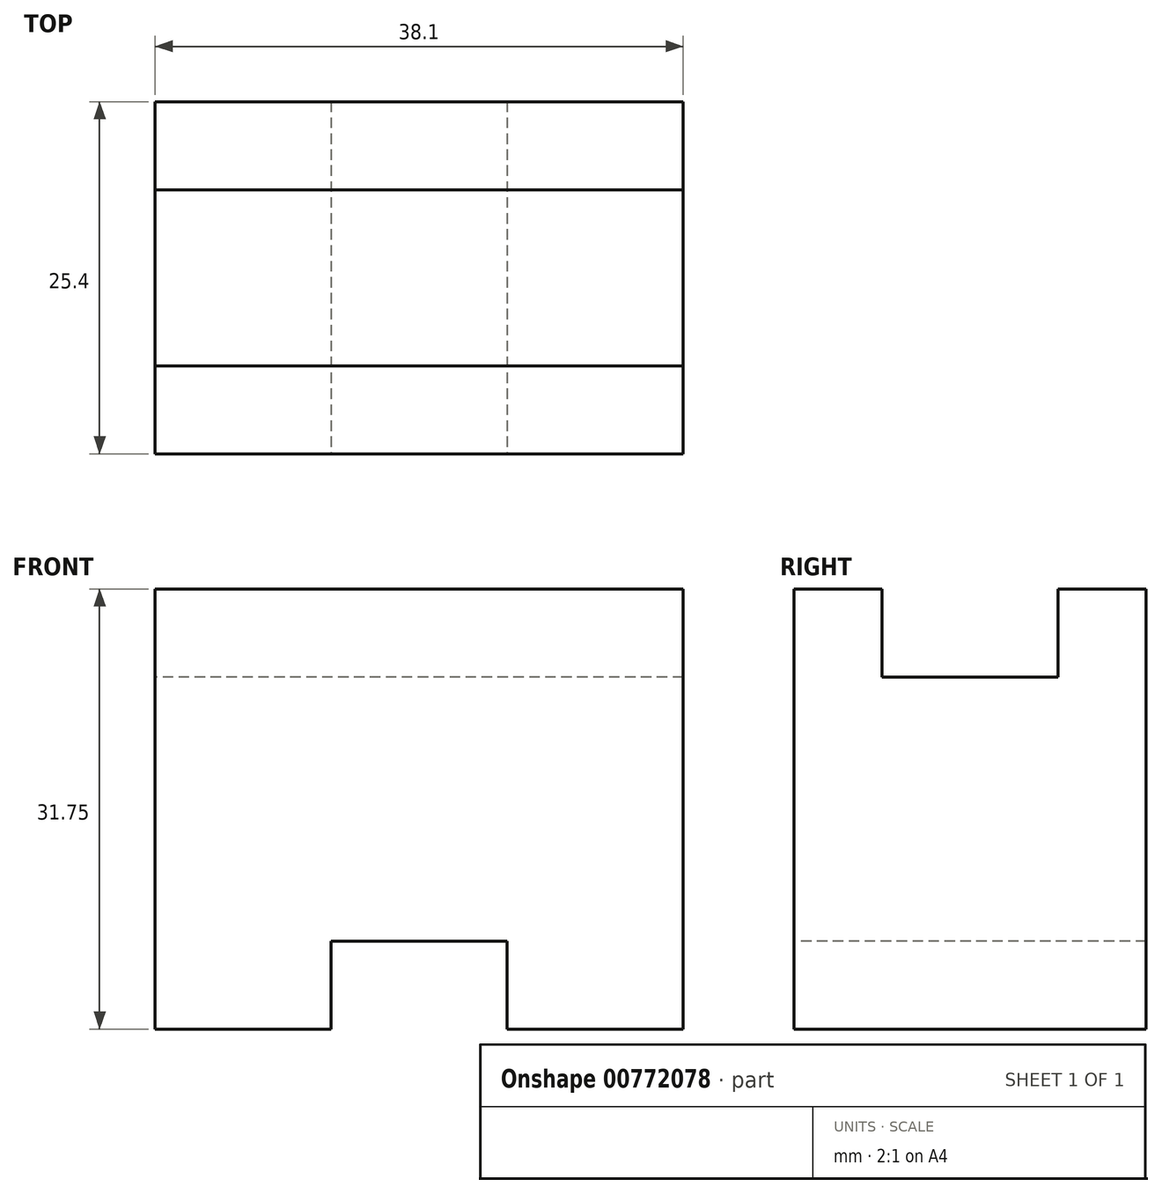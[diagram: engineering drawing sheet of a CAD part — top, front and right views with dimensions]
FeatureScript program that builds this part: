
annotation { "Feature Type Name" : "Feature", "Feature Type Description" : "" }
export const myFeature = defineFeature(function(context is Context, id is Id, definition is map)
    precondition{}
    {
        {
            var Q0;
            Q0=qCreatedBy(makeId("Right.planeOp"),FACE);
            var sketch = newSketch(context, id + "F0", { "sketchPlane" : qUnion([Q0])});
            skLineSegment(sketch, "E0", {"start": v(0, 0) * mm, "end": v(25.4, 0) * mm});
            skLineSegment(sketch, "E1", {"start": v(25.4, 0) * mm, "end": v(25.4, 31.75) * mm});
            skLineSegment(sketch, "E2", {"start": v(25.4, 31.75) * mm, "end": v(19.05, 31.75) * mm});
            skLineSegment(sketch, "E3", {"start": v(19.05, 31.75) * mm, "end": v(19.05, 25.4) * mm});
            skLineSegment(sketch, "E4", {"start": v(19.05, 25.4) * mm, "end": v(6.35, 25.4) * mm});
            skLineSegment(sketch, "E5", {"start": v(6.35, 25.4) * mm, "end": v(6.35, 31.75) * mm});
            skLineSegment(sketch, "E6", {"start": v(6.35, 31.75) * mm, "end": v(0, 31.75) * mm});
            skLineSegment(sketch, "E7", {"start": v(0, 31.75) * mm, "end": v(0, 0) * mm});
            skSolve(sketch);
        }
        {
            var Q0;
            Q0 = qSketchRegion(id + "F0", true);
            extrude(context, id + "F1", {"entities" : qUnion([Q0]), "depth" : 38.1 * mm, "offsetDistance" : 25.4 * mm});
        }
        {
            var Q0;
            Q0=makeQuery(id+"F1.opExtrude","SWEPT_FACE",FACE,{"disambiguationData":[OSD([sQuery(id+"F0.wireOp",EDGE,"E7")])]});
            var sketch = newSketch(context, id + "F2", { "sketchPlane" : qUnion([Q0])});
            skLineSegment(sketch, "E8", {"start": v(0, 0) * mm, "end": v(12.7, 0) * mm});
            skLineSegment(sketch, "E9", {"start": v(12.7, 0) * mm, "end": v(12.7, 6.35) * mm});
            skLineSegment(sketch, "E10", {"start": v(12.7, 6.35) * mm, "end": v(25.4, 6.35) * mm});
            skLineSegment(sketch, "E11", {"start": v(25.4, 6.35) * mm, "end": v(25.4, 0) * mm});
            skLineSegment(sketch, "E12", {"start": v(25.4, 0) * mm, "end": v(38.1, 0) * mm});
            skSolve(sketch);
        }
        {
            var Q0;
            {var subQ0=sQuery(id+"F2.wireOp",EDGE,"E9");Q0=makeQuery(id+"F2.imprint","IMPRINT",FACE,{"disambiguationData":[TD([[makeQuery(id+"F2.imprint","IMPRINT",EDGE,{"derivedFrom":subQ0}),-1.0]])]});}
            extrude(context, id + "F3", {"entities" : qUnion([Q0]), "operationType" : NewBodyOperationType.REMOVE, "oppositeDirection" : true, "depth" : 25.4 * mm, "offsetDistance" : 25.4 * mm});
        }
    });
